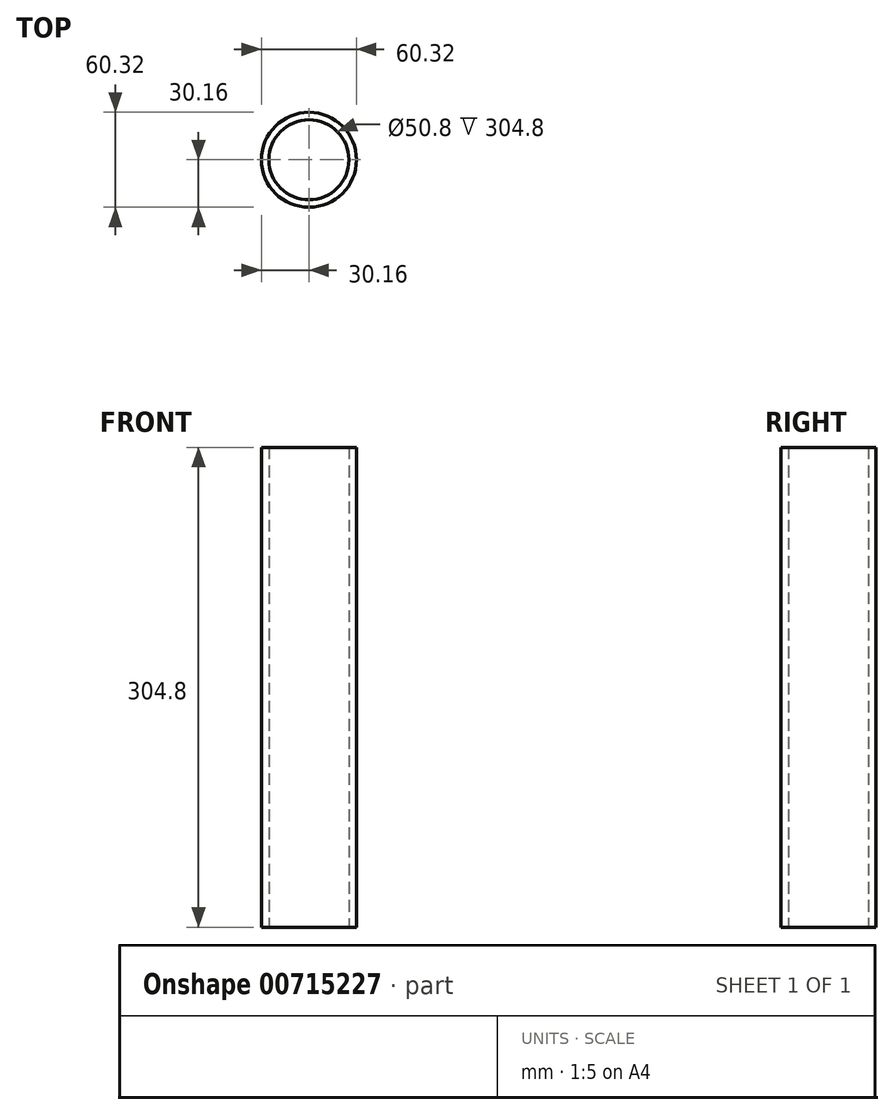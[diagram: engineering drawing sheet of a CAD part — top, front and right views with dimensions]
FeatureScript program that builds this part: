
annotation { "Feature Type Name" : "Feature", "Feature Type Description" : "" }
export const myFeature = defineFeature(function(context is Context, id is Id, definition is map)
    precondition{}
    {
        {
            var Q0;
            Q0=qCreatedBy(makeId("Top.planeOp"),FACE);
            var sketch = newSketch(context, id + "F0", { "sketchPlane" : qUnion([Q0])});
            skCircle(sketch, "E0", {"center": v(0, 0) * mm, "radius": 25.4 * mm});
            skCircle(sketch, "E1", {"center": v(0, 0) * mm, "radius": 30.16 * mm});
            skSolve(sketch);
        }
        {
            var Q0;
            Q0 = qSketchRegion(id + "F0", true);
            extrude(context, id + "F1", {"entities" : qUnion([Q0]), "endBound" : BoundingType.SYMMETRIC, "depth" : 304.8 * mm, "offsetDistance" : 25.4 * mm});
        }
    });
